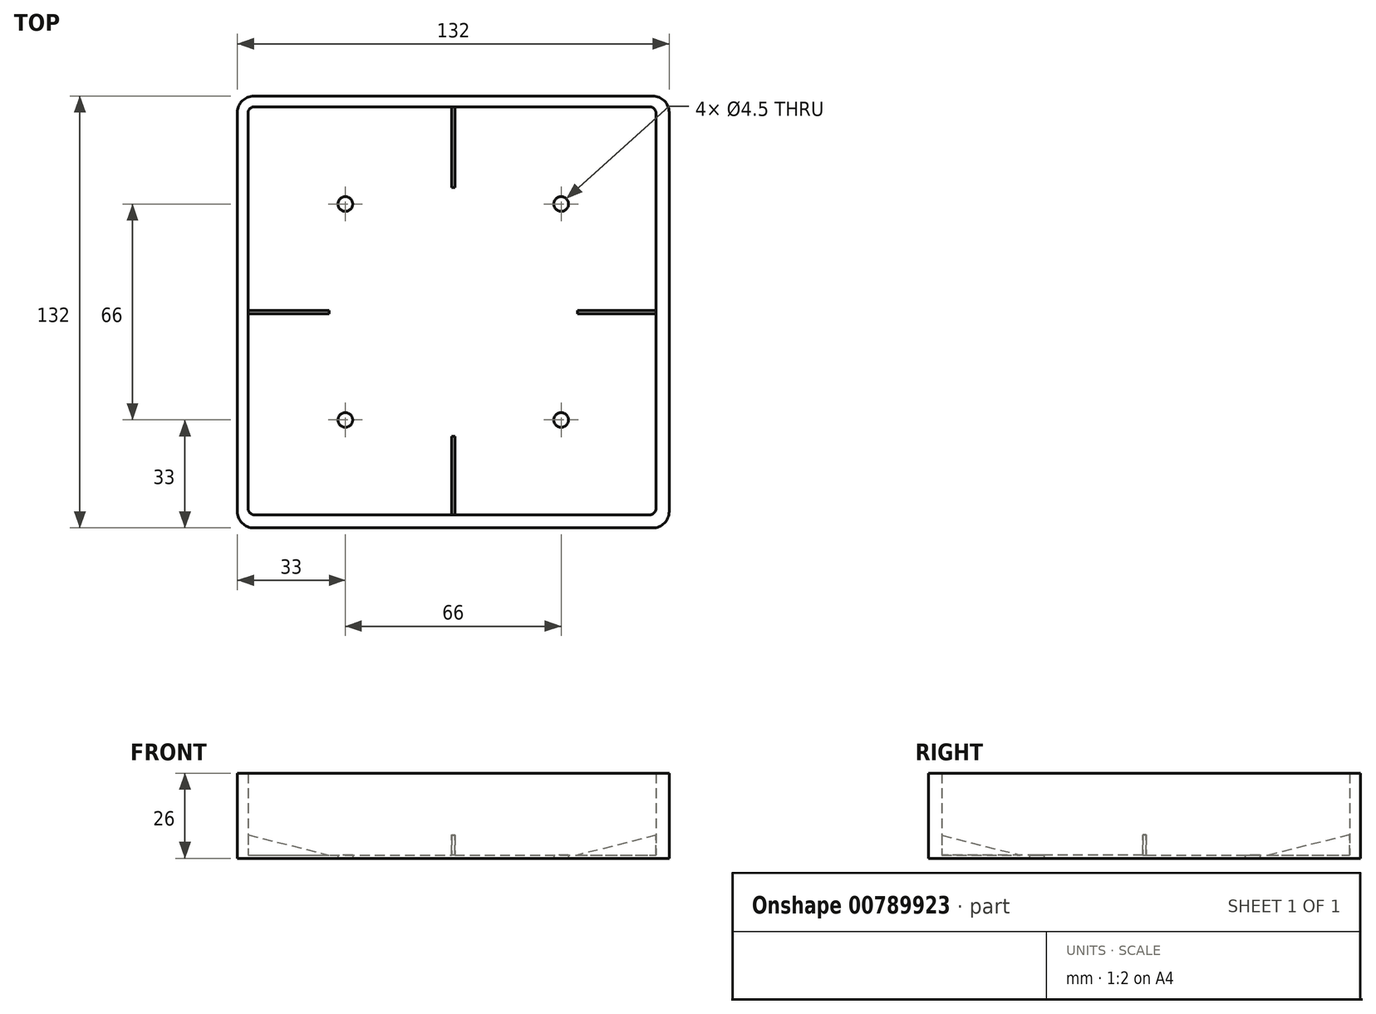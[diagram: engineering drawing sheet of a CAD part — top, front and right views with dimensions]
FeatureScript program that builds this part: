
annotation { "Feature Type Name" : "Feature", "Feature Type Description" : "" }
export const myFeature = defineFeature(function(context is Context, id is Id, definition is map)
    precondition{}
    {
        {
            var Q0;
            Q0=qCreatedBy(makeId("Top.planeOp"),FACE);
            var sketch = newSketch(context, id + "F0", { "sketchPlane" : qUnion([Q0])});
            skLineSegment(sketch, "E0", {"start": v(-62.75, -62) * mm, "end": v(62, -62) * mm});
            skLineSegment(sketch, "E1", {"start": v(62, -62) * mm, "end": v(62, 62.75) * mm});
            skLineSegment(sketch, "E2", {"start": v(62, 62.75) * mm, "end": v(-62.75, 62.75) * mm});
            skLineSegment(sketch, "E3", {"start": v(-62.75, 62.75) * mm, "end": v(-62.75, -62) * mm});
            skLineSegment(sketch, "E4", {"start": v(-66, 66) * mm, "end": v(66, 66) * mm});
            skLineSegment(sketch, "E5", {"start": v(66, 66) * mm, "end": v(66, -66) * mm});
            skLineSegment(sketch, "E6", {"start": v(66, -66) * mm, "end": v(-66, -66) * mm});
            skLineSegment(sketch, "E7", {"start": v(-66, -66) * mm, "end": v(-66, 66) * mm});
            skLineSegment(sketch, "E8", {"start": v(-66, 33) * mm, "end": v(76.99, 33) * mm, "construction": true});
            skLineSegment(sketch, "E9", {"start": v(-33, -86.86) * mm, "end": v(-33, 119.18) * mm, "construction": true});
            skCircle(sketch, "E10", {"center": v(-33, 33) * mm, "radius": 2.25 * mm});
            skCircle(sketch, "E11.1.0", {"center": v(-33, -33) * mm, "radius": 2.25 * mm});
            skCircle(sketch, "E11.2.0", {"center": v(33, -33) * mm, "radius": 2.25 * mm});
            skCircle(sketch, "E11.3.0", {"center": v(33, 33) * mm, "radius": 2.25 * mm});
            skPoint(sketch, "E11.center", {"position": v(0, 0) * mm});
            skSolve(sketch);
        }
        {
            var Q0;
            Q0=makeQuery(id+"F0.imprint","IMPRINT",FACE,{"disambiguationData":[TD([[makeQuery(id+"F0.imprint","IMPRINT",EDGE,{"derivedFrom":sQuery(id+"F0.wireOp",EDGE,"E0")}),1.0]])]});
            extrude(context, id + "F1", {"entities" : qUnion([Q0]), "depth" : 1 * mm, "offsetDistance" : 25 * mm});
        }
        {
            var Q0;
            Q0=makeQuery(id+"F0.imprint","IMPRINT",FACE,{"disambiguationData":[TD([[makeQuery(id+"F0.imprint","IMPRINT",EDGE,{"derivedFrom":sQuery(id+"F0.wireOp",EDGE,"E0")}),-1.0]])]});
            extrude(context, id + "F2", {"entities" : qUnion([Q0]), "operationType" : NewBodyOperationType.ADD, "depth" : 26 * mm, "offsetDistance" : 25 * mm});
        }
        {
            var Q0;
            Q0=qCreatedBy(makeId("Right.planeOp"),FACE);
            var sketch = newSketch(context, id + "F3", { "sketchPlane" : qUnion([Q0])});
            skPoint(sketch, "E12.0", {"position": v(-66, 13) * mm});
            skLineSegment(sketch, "E13.0", {"start": v(66, 0) * mm, "end": v(-66, 0) * mm});
            skLineSegment(sketch, "E14.0", {"start": v(-66, 26) * mm, "end": v(-66, 0) * mm});
            skLineSegment(sketch, "E15.0.0", {"start": v(-66, 0) * mm, "end": v(66, 0) * mm});
            skLineSegment(sketch, "E15.0.1", {"start": v(66, 0) * mm, "end": v(66, 26) * mm});
            skLineSegment(sketch, "E15.0.2", {"start": v(66, 26) * mm, "end": v(-66, 26) * mm});
            skLineSegment(sketch, "E16", {"start": v(-66, 8) * mm, "end": v(-34, 0) * mm});
            skLineSegment(sketch, "E17.MirrorCS", {"start": v(66, 8) * mm, "end": v(34, 0) * mm});
            skSolve(sketch);
        }
        {
            var Q0;
            {var subQ3=sQuery(id+"F3.wireOp",EDGE,"E16");Q0=makeQuery(id+"F3.imprint","IMPRINT",FACE,{"disambiguationData":[TD([[makeQuery(id+"F3.imprint","IMPRINT",EDGE,{"derivedFrom":subQ3}),-1.0]])]});}
            var Q1;
            {var subQ3=sQuery(id+"F3.wireOp",EDGE,"E17.MirrorCS");Q1=makeQuery(id+"F3.imprint","IMPRINT",FACE,{"disambiguationData":[TD([[makeQuery(id+"F3.imprint","IMPRINT",EDGE,{"derivedFrom":subQ3}),1.0]])]});}
            extrude(context, id + "F4", {"entities" : qUnion([Q0, Q1]), "operationType" : NewBodyOperationType.ADD, "endBound" : BoundingType.SYMMETRIC, "depth" : 1 * mm, "offsetDistance" : 25 * mm});
        }
        {
            var Q0;
            Q0=qCreatedBy(makeId("Front.planeOp"),FACE);
            var sketch = newSketch(context, id + "F5", { "sketchPlane" : qUnion([Q0])});
            skPoint(sketch, "E18.0", {"position": v(-66, 13) * mm});
            skLineSegment(sketch, "E19.0", {"start": v(-66, 26) * mm, "end": v(-66, 0) * mm});
            skLineSegment(sketch, "E20.0", {"start": v(66, 0) * mm, "end": v(-66, 0) * mm});
            skLineSegment(sketch, "E21", {"start": v(-66, 8) * mm, "end": v(-34, 0) * mm});
            skLineSegment(sketch, "E22.MirrorCS", {"start": v(66, 8) * mm, "end": v(34, 0) * mm});
            skLineSegment(sketch, "E23", {"start": v(66, 8) * mm, "end": v(66, 0) * mm});
            skLineSegment(sketch, "E24", {"start": v(34, 0) * mm, "end": v(66, 0) * mm});
            skSolve(sketch);
        }
        {
            var Q0;
            {var subQ0=sQuery(id+"F5.wireOp",EDGE,"E22.MirrorCS");var subQ5=sQuery(id+"F5.wireOp",EDGE,"E21");Q0=qUnion([makeQuery(id+"F5.imprint","IMPRINT",FACE,{"disambiguationData":[TD([[makeQuery(id+"F5.imprint","IMPRINT",EDGE,{"derivedFrom":subQ5}),-1.0]])]}),makeQuery(id+"F5.imprint","IMPRINT",FACE,{"disambiguationData":[TD([[makeQuery(id+"F5.imprint","IMPRINT",EDGE,{"derivedFrom":subQ0}),1.0]])]})]);}
            extrude(context, id + "F6", {"entities" : qUnion([Q0]), "operationType" : NewBodyOperationType.ADD, "endBound" : BoundingType.SYMMETRIC, "depth" : 1 * mm, "offsetDistance" : 25 * mm});
        }
        {
            var Q0;
            Q0=makeQuery(id+"F2.opExtrude","SWEPT_EDGE",EDGE,{"disambiguationData":[OSD([sQuery(id+"F0.wireOp",EDGE,"E2"),sQuery(id+"F0.wireOp",EDGE,"E3")])]});
            var Q1;
            Q1=makeQuery(id+"F2.opExtrude","SWEPT_EDGE",EDGE,{"disambiguationData":[OSD([sQuery(id+"F0.wireOp",EDGE,"E1"),sQuery(id+"F0.wireOp",EDGE,"E2")])]});
            var Q2;
            Q2=makeQuery(id+"F2.opExtrude","SWEPT_EDGE",EDGE,{"disambiguationData":[OSD([sQuery(id+"F0.wireOp",EDGE,"E0"),sQuery(id+"F0.wireOp",EDGE,"E1")])]});
            var Q3;
            Q3=makeQuery(id+"F2.opExtrude","SWEPT_EDGE",EDGE,{"disambiguationData":[OSD([sQuery(id+"F0.wireOp",EDGE,"E0"),sQuery(id+"F0.wireOp",EDGE,"E3")])]});
            fillet(context, id + "F7", {"entities" : qUnion([Q0, Q1, Q2, Q3]), "radius" : 2 * mm, "tangentPropagation" : true, "allowEdgeOverflow" : false});
        }
        {
            var Q0;
            Q0=makeQuery(id+"F2.opExtrude","SWEPT_EDGE",EDGE,{"disambiguationData":[OSD([sQuery(id+"F0.wireOp",EDGE,"E6"),sQuery(id+"F0.wireOp",EDGE,"E7")])]});
            var Q1;
            Q1=makeQuery(id+"F2.opExtrude","SWEPT_EDGE",EDGE,{"disambiguationData":[OSD([sQuery(id+"F0.wireOp",EDGE,"E5"),sQuery(id+"F0.wireOp",EDGE,"E6")])]});
            var Q2;
            Q2=makeQuery(id+"F2.opExtrude","SWEPT_EDGE",EDGE,{"disambiguationData":[OSD([sQuery(id+"F0.wireOp",EDGE,"E4"),sQuery(id+"F0.wireOp",EDGE,"E5")])]});
            var Q3;
            Q3=makeQuery(id+"F2.opExtrude","SWEPT_EDGE",EDGE,{"disambiguationData":[OSD([sQuery(id+"F0.wireOp",EDGE,"E4"),sQuery(id+"F0.wireOp",EDGE,"E7")])]});
            fillet(context, id + "F8", {"entities" : qUnion([Q0, Q1, Q2, Q3]), "radius" : 5 * mm, "tangentPropagation" : true, "allowEdgeOverflow" : false});
        }
    });
